# Revit family: ECLLED - Non-Hosted_R16
name_source: partatom
category: Lighting Fixtures
revit_build: Autodesk Revit 2016 (Build: 20150714_1515(x64)
units: mm (PartAtom-declared; Revit-internal decimal feet)

## family parameters
Always vertical = Yes
Cut with Voids When Loaded = No
Light Source = Yes
OmniClass Number = 23.80.70.00
OmniClass Title = Lighting
Part Type = Normal
Room Calculation Point = No
Round Connector Dimension = Use Diameter
Shared = No
Work Plane-Based = No

## types (1)
- ECLLED - Non-Hosted_R16
    AS2293 Classification = C0=D32 C90=D32
    Catalogue Number = ECLLED
    Charging Method = Constant Rate<0.05C
    Color Filter = 16777215
    Construction = Polycarbonate base and Opal Acrylic diffuser
    Description = Economy LED Circlite emergency
    Diffuser = Opal Acrylic
    Dimensions L x W x H = 340mm(Diameter)x100mm(Height)
    Dimming Lamp Color Temperature Shift = <None>
    IP Rating = IP44
    Lamp(s) = LED panel array (30,000hours), 4000K, Ra<80
    Mounting = Surface mount
    Operating Mode = Maintained
    Operating Voltage = 250V AC; 50Hz
    Operating temperature = 1C° to 40 C°
    Photometric Web File = 686_Circlite_LED_ECLLED_Production_Sample_7246mVDC_24062016-02_Revised.ies
    Power consumption = 15.9 Watts
    Testing System = N/A - Manual test switch
    Tilt Angle = 90.00°
    Total lumen output = 1340 lm

## geometry (parser evidence)
native form markers: Sweep x1
no freeform markers — native parametric forms only
